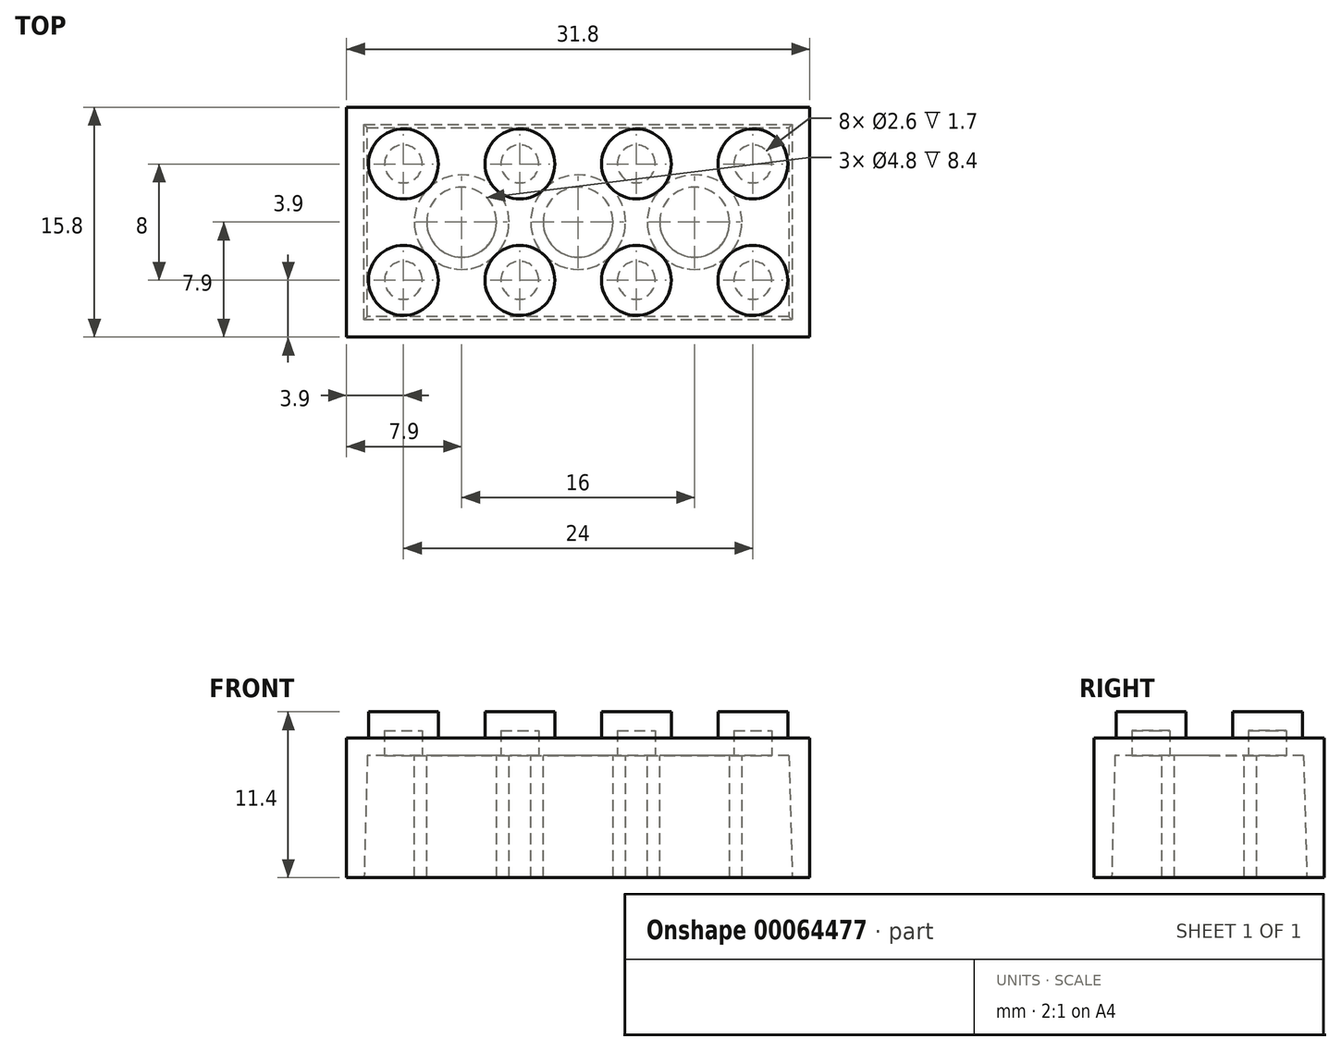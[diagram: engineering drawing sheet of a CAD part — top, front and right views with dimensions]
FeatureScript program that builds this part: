
annotation { "Feature Type Name" : "Feature", "Feature Type Description" : "" }
export const myFeature = defineFeature(function(context is Context, id is Id, definition is map)
    precondition{}
    {
        {
            var Q0;
            Q0=qCreatedBy(makeId("Top.planeOp"),FACE);
            var sketch = newSketch(context, id + "F0", { "sketchPlane" : qUnion([Q0])});
            skLineSegment(sketch, "E0.rect.bottom", {"start": v(15.9, -7.9) * mm, "end": v(-15.9, -7.9) * mm});
            skLineSegment(sketch, "E0.rect.top", {"start": v(15.9, 7.9) * mm, "end": v(-15.9, 7.9) * mm});
            skLineSegment(sketch, "E0.rect.left", {"start": v(15.9, -7.9) * mm, "end": v(15.9, 7.9) * mm});
            skLineSegment(sketch, "E0.rect.right", {"start": v(-15.9, -7.9) * mm, "end": v(-15.9, 7.9) * mm});
            skPoint(sketch, "E0.rect.middle", {"position": v(0, 0) * mm});
            skSolve(sketch);
        }
        {
            var Q0;
            Q0=makeQuery(id+"F0.imprint","IMPRINT",FACE,{"disambiguationData":[TD([[makeQuery(id+"F0.imprint","IMPRINT",EDGE,{"derivedFrom":sQuery(id+"F0.wireOp",EDGE,"E0.rect.bottom")}),-1.0]])]});
            extrude(context, id + "F1", {"entities" : qUnion([Q0]), "depth" : 9.6 * mm});
        }
        {
            var Q0;
            Q0=makeQuery(id+"F1.opExtrude","CAP_FACE",FACE,{"disambiguationData":[OSD([sQuery(id+"F0.wireOp",EDGE,"E0.rect.bottom"),sQuery(id+"F0.wireOp",EDGE,"E0.rect.top"),sQuery(id+"F0.wireOp",EDGE,"E0.rect.left"),sQuery(id+"F0.wireOp",EDGE,"E0.rect.right")])],"isStart":false});
            var sketch = newSketch(context, id + "F2", { "sketchPlane" : qUnion([Q0])});
            skCircle(sketch, "E1", {"center": v(-12, 4) * mm, "radius": 2.4 * mm});
            skCircle(sketch, "E2.0.1.0", {"center": v(-12, -4) * mm, "radius": 2.4 * mm});
            skCircle(sketch, "E2.1.0.0", {"center": v(-4, 4) * mm, "radius": 2.4 * mm});
            skCircle(sketch, "E2.1.1.0", {"center": v(-4, -4) * mm, "radius": 2.4 * mm});
            skCircle(sketch, "E2.2.0.0", {"center": v(4, 4) * mm, "radius": 2.4 * mm});
            skCircle(sketch, "E2.2.1.0", {"center": v(4, -4) * mm, "radius": 2.4 * mm});
            skCircle(sketch, "E2.3.0.0", {"center": v(12, 4) * mm, "radius": 2.4 * mm});
            skCircle(sketch, "E2.3.1.0", {"center": v(12, -4) * mm, "radius": 2.4 * mm});
            skLineSegment(sketch, "E2.direction1", {"start": v(-12, 4) * mm, "end": v(-4, 4) * mm, "construction": true});
            skLineSegment(sketch, "E2.direction2", {"start": v(-12, 4) * mm, "end": v(-12, -4) * mm, "construction": true});
            skSolve(sketch);
        }
        {
            var Q0;
            Q0=makeQuery(id+"F2.imprint","IMPRINT",FACE,{"disambiguationData":[TD([[makeQuery(id+"F2.imprint","IMPRINT",EDGE,{"derivedFrom":sQuery(id+"F2.wireOp",EDGE,"E1")}),1.0]])]});
            var Q1;
            Q1=makeQuery(id+"F2.imprint","IMPRINT",FACE,{"disambiguationData":[TD([[makeQuery(id+"F2.imprint","IMPRINT",EDGE,{"derivedFrom":sQuery(id+"F2.wireOp",EDGE,"E2.0.1.0")}),1.0]])]});
            var Q2;
            Q2=makeQuery(id+"F2.imprint","IMPRINT",FACE,{"disambiguationData":[TD([[makeQuery(id+"F2.imprint","IMPRINT",EDGE,{"derivedFrom":sQuery(id+"F2.wireOp",EDGE,"E2.1.0.0")}),1.0]])]});
            var Q3;
            Q3=makeQuery(id+"F2.imprint","IMPRINT",FACE,{"disambiguationData":[TD([[makeQuery(id+"F2.imprint","IMPRINT",EDGE,{"derivedFrom":sQuery(id+"F2.wireOp",EDGE,"E2.1.1.0")}),1.0]])]});
            var Q4;
            Q4=makeQuery(id+"F2.imprint","IMPRINT",FACE,{"disambiguationData":[TD([[makeQuery(id+"F2.imprint","IMPRINT",EDGE,{"derivedFrom":sQuery(id+"F2.wireOp",EDGE,"E2.2.0.0")}),1.0]])]});
            var Q5;
            Q5=makeQuery(id+"F2.imprint","IMPRINT",FACE,{"disambiguationData":[TD([[makeQuery(id+"F2.imprint","IMPRINT",EDGE,{"derivedFrom":sQuery(id+"F2.wireOp",EDGE,"E2.2.1.0")}),1.0]])]});
            var Q6;
            Q6=makeQuery(id+"F2.imprint","IMPRINT",FACE,{"disambiguationData":[TD([[makeQuery(id+"F2.imprint","IMPRINT",EDGE,{"derivedFrom":sQuery(id+"F2.wireOp",EDGE,"E2.3.0.0")}),1.0]])]});
            var Q7;
            Q7=makeQuery(id+"F2.imprint","IMPRINT",FACE,{"disambiguationData":[TD([[makeQuery(id+"F2.imprint","IMPRINT",EDGE,{"derivedFrom":sQuery(id+"F2.wireOp",EDGE,"E2.3.1.0")}),1.0]])]});
            extrude(context, id + "F3", {"entities" : qUnion([Q0, Q1, Q2, Q3, Q4, Q5, Q6, Q7]), "operationType" : NewBodyOperationType.ADD, "depth" : 1.8 * mm});
        }
        {
            var Q0;
            Q0=makeQuery(id+"F1.opExtrude","CAP_FACE",FACE,{"disambiguationData":[OSD([sQuery(id+"F0.wireOp",EDGE,"E0.rect.bottom"),sQuery(id+"F0.wireOp",EDGE,"E0.rect.top"),sQuery(id+"F0.wireOp",EDGE,"E0.rect.left"),sQuery(id+"F0.wireOp",EDGE,"E0.rect.right")])],"isStart":true});
            var sketch = newSketch(context, id + "F4", { "sketchPlane" : qUnion([Q0])});
            skLineSegment(sketch, "E3.0", {"start": v(14.7, 6.7) * mm, "end": v(-14.7, 6.7) * mm});
            skLineSegment(sketch, "E3.1", {"start": v(14.7, -6.7) * mm, "end": v(14.7, 6.7) * mm});
            skLineSegment(sketch, "E3.2", {"start": v(-14.7, -6.7) * mm, "end": v(14.7, -6.7) * mm});
            skLineSegment(sketch, "E3.3", {"start": v(-14.7, 6.7) * mm, "end": v(-14.7, -6.7) * mm});
            skSolve(sketch);
        }
        {
            var Q0;
            Q0=makeQuery(id+"F4.imprint","IMPRINT",FACE,{"disambiguationData":[TD([[makeQuery(id+"F4.imprint","IMPRINT",EDGE,{"derivedFrom":sQuery(id+"F4.wireOp",EDGE,"E3.0")}),1.0]])]});
            extrude(context, id + "F5", {"entities" : qUnion([Q0]), "operationType" : NewBodyOperationType.REMOVE, "oppositeDirection" : true, "depth" : 8.4 * mm, "hasDraft" : true, "draftAngle" : 1.5 * degree, "draftPullDirection" : true});
        }
        {
            var Q0;
            Q0=makeQuery(id+"F5.boolean.opBoolean","COPY",FACE,{"derivedFrom":makeQuery(id+"F5.opExtrude","CAP_FACE",FACE,{"disambiguationData":[OSD([sQuery(id+"F4.wireOp",EDGE,"E3.0"),sQuery(id+"F4.wireOp",EDGE,"E3.1"),sQuery(id+"F4.wireOp",EDGE,"E3.2"),sQuery(id+"F4.wireOp",EDGE,"E3.3")])],"isStart":false})});
            var sketch = newSketch(context, id + "F6", { "sketchPlane" : qUnion([Q0])});
            skCircle(sketch, "E4.0.0", {"center": v(12, 4) * mm, "radius": 2.4 * mm, "construction": true});
            skCircle(sketch, "E5.0.0", {"center": v(4, 4) * mm, "radius": 2.4 * mm, "construction": true});
            skCircle(sketch, "E6.0.0", {"center": v(-4, 4) * mm, "radius": 2.4 * mm, "construction": true});
            skCircle(sketch, "E7.0.0", {"center": v(-4, -4) * mm, "radius": 2.4 * mm, "construction": true});
            skCircle(sketch, "E8.0.0", {"center": v(4, -4) * mm, "radius": 2.4 * mm, "construction": true});
            skCircle(sketch, "E9.0.0", {"center": v(12, -4) * mm, "radius": 2.4 * mm, "construction": true});
            skCircle(sketch, "E10.0.0", {"center": v(-12, -4) * mm, "radius": 2.4 * mm, "construction": true});
            skCircle(sketch, "E11.0.0", {"center": v(-12, 4) * mm, "radius": 2.4 * mm, "construction": true});
            skCircle(sketch, "E12", {"center": v(-12, 4) * mm, "radius": 1.3 * mm});
            skCircle(sketch, "E13", {"center": v(-4, 4) * mm, "radius": 1.3 * mm});
            skCircle(sketch, "E14", {"center": v(4, 4) * mm, "radius": 1.3 * mm});
            skCircle(sketch, "E15", {"center": v(12, 4) * mm, "radius": 1.3 * mm});
            skCircle(sketch, "E16", {"center": v(12, -4) * mm, "radius": 1.3 * mm});
            skCircle(sketch, "E17", {"center": v(4, -4) * mm, "radius": 1.3 * mm});
            skCircle(sketch, "E18", {"center": v(-4, -4) * mm, "radius": 1.3 * mm});
            skCircle(sketch, "E19", {"center": v(-12, -4) * mm, "radius": 1.3 * mm});
            skSolve(sketch);
        }
        {
            var Q0;
            Q0 = qSketchRegion(id + "F6", true);
            extrude(context, id + "F7", {"entities" : qUnion([Q0]), "operationType" : NewBodyOperationType.REMOVE, "oppositeDirection" : true, "depth" : 1.7 * mm});
        }
        {
            var Q0;
            Q0=makeQuery(id+"F5.boolean.opBoolean","COPY",FACE,{"derivedFrom":makeQuery(id+"F5.opExtrude","CAP_FACE",FACE,{"disambiguationData":[OSD([sQuery(id+"F4.wireOp",EDGE,"E3.0"),sQuery(id+"F4.wireOp",EDGE,"E3.1"),sQuery(id+"F4.wireOp",EDGE,"E3.2"),sQuery(id+"F4.wireOp",EDGE,"E3.3")])],"isStart":false})});
            var sketch = newSketch(context, id + "F8", { "sketchPlane" : qUnion([Q0])});
            skLineSegment(sketch, "E20", {"start": v(-15.9, 0) * mm, "end": v(15.9, 0) * mm, "construction": true});
            skCircle(sketch, "E21", {"center": v(0, 0) * mm, "radius": 3.25 * mm});
            skCircle(sketch, "E22", {"center": v(8, 0) * mm, "radius": 3.25 * mm});
            skCircle(sketch, "E23", {"center": v(-8, 0) * mm, "radius": 3.25 * mm});
            skCircle(sketch, "E24.0", {"center": v(-12, 4) * mm, "radius": 1.3 * mm, "construction": true});
            skCircle(sketch, "E25.0", {"center": v(-4, -4) * mm, "radius": 1.3 * mm, "construction": true});
            skLineSegment(sketch, "E26", {"start": v(-12, 4) * mm, "end": v(-4, -4) * mm, "construction": true});
            skCircle(sketch, "E27", {"center": v(-8, 0) * mm, "radius": 2.4 * mm});
            skCircle(sketch, "E28", {"center": v(0, 0) * mm, "radius": 2.4 * mm});
            skCircle(sketch, "E29", {"center": v(8, 0) * mm, "radius": 2.4 * mm});
            skSolve(sketch);
        }
        {
            var Q0;
            Q0 = qSketchRegion(id + "F8", true);
            var Q1;
            Q1=makeQuery(id+"F1.opExtrude","CAP_FACE",FACE,{"disambiguationData":[OSD([sQuery(id+"F0.wireOp",EDGE,"E0.rect.bottom"),sQuery(id+"F0.wireOp",EDGE,"E0.rect.top"),sQuery(id+"F0.wireOp",EDGE,"E0.rect.left"),sQuery(id+"F0.wireOp",EDGE,"E0.rect.right")])],"isStart":true});
            extrude(context, id + "F9", {"entities" : qUnion([Q0]), "operationType" : NewBodyOperationType.ADD, "endBound" : BoundingType.UP_TO_SURFACE, "endBoundEntityFace" : qUnion([Q1]), "depth" : 25 * mm});
        }
    });
